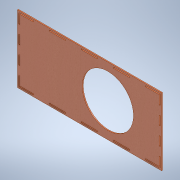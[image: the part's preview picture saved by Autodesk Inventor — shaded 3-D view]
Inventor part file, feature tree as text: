
AUTODESK INVENTOR PART (.ipt)
format: ipt  version: 2020.2 (Build 242310000, 310)  size: 226,816 bytes
history: native  units: mm
features: sketch x2, extrude x2, other x1
ambient origin geometry x8: Origin, YZ Plane, XZ Plane, XY Plane, X Axis, Y Axis, Z Axis, Center Point
bodies: Body1 (feature_tree)
feature tree (5):
  other  "Sólido1"
  sketch  "Boceto1"  dims[d3=3.0mm d4=0.0mm d5=3.0mm d6=0.0mm]
  sketch  "Boceto2"  dims[d8=210.0mm d9=210.0mm d10=5.0mm d11=27.72mm d12=5.0mm d13=5.0mm d14=450.0mm d15=5.0mm d16=5.0mm d17=5.0mm d18=45.0mm d19=30.71mm d20=3.0mm d21=3.0mm d22=30.71mm d23=45.0mm d24=3.0mm d25=3.0mm d26=5.0mm d27=5.0mm d29=5.0mm d30=30.71mm d31=45.0mm d32=5.0mm d33=3.0mm d34=3.0mm d35=5.0mm d36=5.0mm d37=45.0mm d38=30.71mm d39=3.0mm d40=3.0mm d41=50.0mm d42=5.0mm d43=5.0mm d44=5.0mm d45=3.0mm d46=3.0mm]
  extrude  "Extrusión1"  Depth=3.0mm TaperAngle=0.0deg
  extrude  "Extrusión2"  Depth=210.0mm
